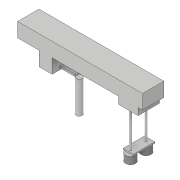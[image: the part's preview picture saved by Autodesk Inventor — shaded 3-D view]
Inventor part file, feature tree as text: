
AUTODESK INVENTOR PART (.ipt)
format: ipt  version: 2019 (Build 230136000, 136)  size: 195,072 bytes
history: native  units: in
note: dims shown in document units (in); Inventor stores cm internally (conversion verified against a paired STEP export)
features: sketch x18, extrude x17, thread x3
ambient origin geometry x8: Origin, YZ Plane, XZ Plane, XY Plane, X Axis, Y Axis, Z Axis, Center Point
bodies: Solid1 (feature_tree)
feature tree (38):
  extrude  "Extrusion1"  Depth=7.874in
  extrude  "Extrusion2"  Depth=5.9055in TaperAngle=0.0deg
  extrude  "Extrusion3"  Depth=7.874in TaperAngle=0.0deg
  extrude  "Extrusion4"  Depth=7.874in TaperAngle=0.0deg
  sketch  "Sketch5"  dims[d14=7.874in d15=0.0in d16=17.7165in d17=0.0in]
  extrude  "Extrusion5"  Depth=17.7165in TaperAngle=0.0deg
  extrude  "Extrusion6"  Depth=3.937in TaperAngle=0.0deg
  extrude  "Extrusion7"  Depth=19.685in TaperAngle=0.0deg
  extrude  "Extrusion8"  Depth=0.3937in TaperAngle=0.0deg
  extrude  "Extrusion9"  Depth=3.937in TaperAngle=0.0deg
  extrude  "Extrusion10"  Depth=3.937in TaperAngle=0.0deg
  extrude  "Extrusion11"  Depth=39.3701in TaperAngle=0.0deg
  extrude  "Extrusion12"  [1 undecoded]
  extrude  "Extrusion13"  [1 undecoded]
  extrude  "Extrusion14"  [1 undecoded]
  extrude  "Extrusion15"  [1 undecoded]
  extrude  "Extrusion16"  [1 undecoded]
  extrude  "Extrusion17"  [1 undecoded]
  thread  "Thread1"  [1 undecoded]
  thread  "Thread2"  [1 undecoded]
  thread  "Thread3"  [1 undecoded]
  sketch  "Sketch1"  dims[d0=68.8976in d1=7.874in]
  sketch  "Sketch2"  dims[d2=11.811in d3=0.0in d4=5.9055in d5=0.0in]
  sketch  "Sketch3"  dims[d6=5.9055in d7=0.0in d8=7.874in d9=0.0in]
  sketch  "Sketch4"  dims[d10=6.6929in d11=0.0in d12=7.874in d13=0.0in]
  sketch  "Sketch6"  dims[d18=9.8425in d19=0.0in d20=3.937in d21=0.0in]
  sketch  "Sketch7"  dims[d22=19.685in d23=0.0in d24=19.685in d25=0.0in]
  sketch  "Sketch8"  dims[d26=0.7874in d27=0.0in d28=0.3937in d29=0.0in]
  sketch  "Sketch9"  dims[d30=0.3937in d31=0.0in d32=3.937in d33=0.0in]
  sketch  "Sketch10"  dims[d34=3.937in d35=0.0in d36=39.3701in d37=0.0in]
  sketch  "Sketch11"  dims[d38=39.3701in d39=0.0in d40=39.3701in d41=0.0in]
  sketch  "Sketch12"
  sketch  "Sketch13"
  sketch  "Sketch14"
  sketch  "Sketch15"
  sketch  "Sketch16"
  sketch  "Sketch17"
  sketch  "Sketch18"
note: 9 required parameter values undecoded (feature->parameter linkage not recoverable at this tier; creation-order binding heuristic only, values carry confidence <= 0.55)
